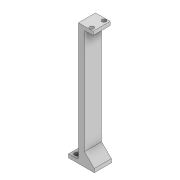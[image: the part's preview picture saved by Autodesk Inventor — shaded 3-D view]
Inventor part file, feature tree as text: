
AUTODESK INVENTOR PART (.ipt)
format: ipt  version: 2022 (Build 260153000, 153)  size: 130,048 bytes
history: native  units: mm
features: sketch x5, extrude x3, hole x2, chamfer x2
ambient origin geometry x8: Origin, YZ Plane, XZ Plane, XY Plane, X Axis, Y Axis, Z Axis, Center Point
bodies: Solid1 (feature_tree)
feature tree (12):
  extrude  "Extrusion1"  Depth=100.0mm
  extrude  "Extrusion2"  Depth=7.0mm
  hole  "Hole1"  [1 undecoded]
  extrude  "Extrusion3"  Depth=2.0mm
  hole  "Hole2"  [1 undecoded]
  chamfer  "Chamfer1"  Distance=8.0mm
  chamfer  "Chamfer2"  Distance=3.0mm
  sketch  "Sketch1"  dims[d0=5.0mm d1=100.0mm]
  sketch  "Sketch2"  dims[d2=14.0mm d3=0.0mm d5=7.0mm]
  sketch  "Sketch3"  dims[d6=3.0mm d7=0.0mm d8=3.0mm]
  sketch  "Sketch4"  dims[d9=2.0mm d10=2.0mm]
  sketch  "Sketch5"  dims[d11=3.4mm d12=6.0mm d13=4.0mm d14=2.0mm d15=90.0deg d16=8.0mm d17=20.594885mm d18=8.0mm d20=8.0mm d21=3.0mm d22=0.0mm d23=8.0mm d24=3.5mm d25=3.4mm d26=6.0mm d27=4.0mm d28=2.0mm d29=90.0deg d30=8.0mm d31=20.594885mm d32=8.0mm d33=2.0mm d34=45.0deg d35=1.0mm d36=2.0mm d37=45.0deg]
note: 2 required parameter values undecoded (feature->parameter linkage not recoverable at this tier; creation-order binding heuristic only, values carry confidence <= 0.55)
